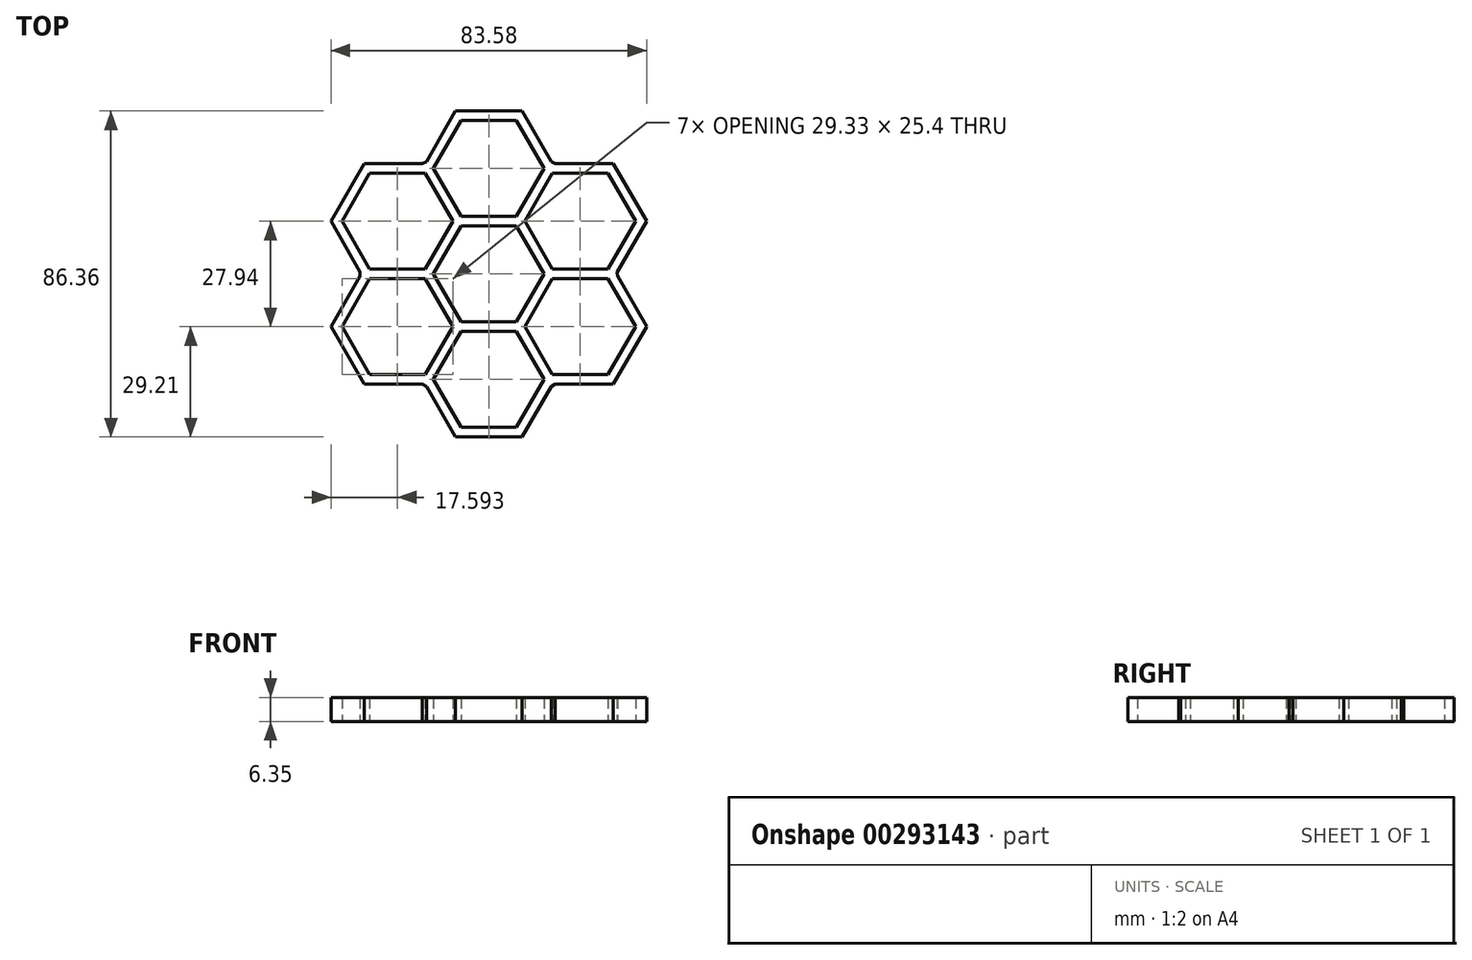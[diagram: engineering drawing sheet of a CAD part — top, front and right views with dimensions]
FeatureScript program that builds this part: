
annotation { "Feature Type Name" : "Feature", "Feature Type Description" : "" }
export const myFeature = defineFeature(function(context is Context, id is Id, definition is map)
    precondition{}
    {
        {
            var Q0;
            Q0=qCreatedBy(makeId("Top.planeOp"),FACE);
            var sketch = newSketch(context, id + "F0", { "sketchPlane" : qUnion([Q0])});
            skCircle(sketch, "E0.cCircle", {"center": v(0, 0) * mm, "radius": 12.7 * mm, "construction": true});
            skLineSegment(sketch, "E0.0", {"start": v(7.33, -12.7) * mm, "end": v(-7.33, -12.7) * mm});
            skLineSegment(sketch, "E0.1", {"start": v(-7.33, -12.7) * mm, "end": v(-14.66, 0) * mm});
            skLineSegment(sketch, "E0.2", {"start": v(-14.66, 0) * mm, "end": v(-7.33, 12.7) * mm});
            skLineSegment(sketch, "E0.3", {"start": v(-7.33, 12.7) * mm, "end": v(7.33, 12.7) * mm});
            skLineSegment(sketch, "E0.4", {"start": v(7.33, 12.7) * mm, "end": v(14.66, 0) * mm});
            skLineSegment(sketch, "E0.5", {"start": v(14.66, 0) * mm, "end": v(7.33, -12.7) * mm});
            skPoint(sketch, "E0.0.midPoint", {"position": v(0, -12.7) * mm});
            skCircle(sketch, "E1.cCircle", {"center": v(0, 27.94) * mm, "radius": 12.7 * mm, "construction": true});
            skLineSegment(sketch, "E1.0", {"start": v(7.33, 15.24) * mm, "end": v(-7.33, 15.24) * mm});
            skLineSegment(sketch, "E1.1", {"start": v(-7.33, 15.24) * mm, "end": v(-14.66, 27.94) * mm});
            skLineSegment(sketch, "E1.2", {"start": v(-14.66, 27.94) * mm, "end": v(-7.33, 40.64) * mm});
            skLineSegment(sketch, "E1.3", {"start": v(-7.33, 40.64) * mm, "end": v(7.33, 40.64) * mm});
            skLineSegment(sketch, "E1.4", {"start": v(7.33, 40.64) * mm, "end": v(14.66, 27.94) * mm});
            skLineSegment(sketch, "E1.5", {"start": v(14.66, 27.94) * mm, "end": v(7.33, 15.24) * mm});
            skPoint(sketch, "E1.0.midPoint", {"position": v(0, 15.24) * mm});
            skLineSegment(sketch, "E2.1.0", {"start": v(-31.53, 1.27) * mm, "end": v(-38.86, 13.97) * mm});
            skLineSegment(sketch, "E2.1.1", {"start": v(-38.86, 13.97) * mm, "end": v(-31.53, 26.67) * mm});
            skLineSegment(sketch, "E2.1.2", {"start": v(-31.53, 26.67) * mm, "end": v(-16.86, 26.67) * mm});
            skLineSegment(sketch, "E2.1.3", {"start": v(-16.86, 26.67) * mm, "end": v(-9.53, 13.97) * mm});
            skLineSegment(sketch, "E2.1.4", {"start": v(-9.53, 13.97) * mm, "end": v(-16.86, 1.27) * mm});
            skLineSegment(sketch, "E2.1.5", {"start": v(-16.86, 1.27) * mm, "end": v(-31.53, 1.27) * mm});
            skLineSegment(sketch, "E2.2.0", {"start": v(-16.86, -26.67) * mm, "end": v(-31.53, -26.67) * mm});
            skLineSegment(sketch, "E2.2.1", {"start": v(-31.53, -26.67) * mm, "end": v(-38.86, -13.97) * mm});
            skLineSegment(sketch, "E2.2.2", {"start": v(-38.86, -13.97) * mm, "end": v(-31.53, -1.27) * mm});
            skLineSegment(sketch, "E2.2.3", {"start": v(-31.53, -1.27) * mm, "end": v(-16.86, -1.27) * mm});
            skLineSegment(sketch, "E2.2.4", {"start": v(-16.86, -1.27) * mm, "end": v(-9.53, -13.97) * mm});
            skLineSegment(sketch, "E2.2.5", {"start": v(-9.53, -13.97) * mm, "end": v(-16.86, -26.67) * mm});
            skLineSegment(sketch, "E2.3.0", {"start": v(14.66, -27.94) * mm, "end": v(7.33, -40.64) * mm});
            skLineSegment(sketch, "E2.3.1", {"start": v(7.33, -40.64) * mm, "end": v(-7.33, -40.64) * mm});
            skLineSegment(sketch, "E2.3.2", {"start": v(-7.33, -40.64) * mm, "end": v(-14.66, -27.94) * mm});
            skLineSegment(sketch, "E2.3.3", {"start": v(-14.66, -27.94) * mm, "end": v(-7.33, -15.24) * mm});
            skLineSegment(sketch, "E2.3.4", {"start": v(-7.33, -15.24) * mm, "end": v(7.33, -15.24) * mm});
            skLineSegment(sketch, "E2.3.5", {"start": v(7.33, -15.24) * mm, "end": v(14.66, -27.94) * mm});
            skLineSegment(sketch, "E2.4.0", {"start": v(31.53, -1.27) * mm, "end": v(38.86, -13.97) * mm});
            skLineSegment(sketch, "E2.4.1", {"start": v(38.86, -13.97) * mm, "end": v(31.53, -26.67) * mm});
            skLineSegment(sketch, "E2.4.2", {"start": v(31.53, -26.67) * mm, "end": v(16.86, -26.67) * mm});
            skLineSegment(sketch, "E2.4.3", {"start": v(16.86, -26.67) * mm, "end": v(9.53, -13.97) * mm});
            skLineSegment(sketch, "E2.4.4", {"start": v(9.53, -13.97) * mm, "end": v(16.86, -1.27) * mm});
            skLineSegment(sketch, "E2.4.5", {"start": v(16.86, -1.27) * mm, "end": v(31.53, -1.27) * mm});
            skLineSegment(sketch, "E2.5.0", {"start": v(16.86, 26.67) * mm, "end": v(31.53, 26.67) * mm});
            skLineSegment(sketch, "E2.5.1", {"start": v(31.53, 26.67) * mm, "end": v(38.86, 13.97) * mm});
            skLineSegment(sketch, "E2.5.2", {"start": v(38.86, 13.97) * mm, "end": v(31.53, 1.27) * mm});
            skLineSegment(sketch, "E2.5.3", {"start": v(31.53, 1.27) * mm, "end": v(16.86, 1.27) * mm});
            skLineSegment(sketch, "E2.5.4", {"start": v(16.86, 1.27) * mm, "end": v(9.53, 13.97) * mm});
            skLineSegment(sketch, "E2.5.5", {"start": v(9.53, 13.97) * mm, "end": v(16.86, 26.67) * mm});
            skLineSegment(sketch, "E3", {"start": v(31.33, 1.4) * mm, "end": v(31.34, 1.27) * mm});
            skLineSegment(sketch, "E4.0", {"start": v(33, 29.21) * mm, "end": v(41.8, 13.97) * mm});
            skLineSegment(sketch, "E4.1", {"start": v(-17.54, -29.2) * mm, "end": v(-33, -29.2) * mm});
            skLineSegment(sketch, "E4.2", {"start": v(-17.54, -29.21) * mm, "end": v(-16.52, -29.8) * mm});
            skLineSegment(sketch, "E4.3", {"start": v(-8.8, -43.18) * mm, "end": v(-16.52, -29.8) * mm});
            skLineSegment(sketch, "E4.4", {"start": v(8.8, -43.18) * mm, "end": v(-8.8, -43.18) * mm});
            skLineSegment(sketch, "E4.5", {"start": v(16.52, -29.8) * mm, "end": v(8.8, -43.18) * mm});
            skLineSegment(sketch, "E4.6", {"start": v(17.54, -29.21) * mm, "end": v(16.52, -29.8) * mm});
            skLineSegment(sketch, "E4.7", {"start": v(33.95, 0.39) * mm, "end": v(34.02, -0.5) * mm});
            skLineSegment(sketch, "E4.8", {"start": v(34.02, -0.5) * mm, "end": v(41.8, -13.97) * mm});
            skLineSegment(sketch, "E4.9", {"start": v(41.8, -13.97) * mm, "end": v(33, -29.21) * mm});
            skLineSegment(sketch, "E4.10", {"start": v(33, -29.21) * mm, "end": v(17.54, -29.21) * mm});
            skLineSegment(sketch, "E4.11", {"start": v(-33, -29.2) * mm, "end": v(-41.8, -13.97) * mm});
            skLineSegment(sketch, "E4.12", {"start": v(41.8, 13.97) * mm, "end": v(33.95, 0.39) * mm});
            skLineSegment(sketch, "E4.13", {"start": v(-41.8, -13.97) * mm, "end": v(-34.07, -0.59) * mm});
            skLineSegment(sketch, "E4.14", {"start": v(-34.07, 0.59) * mm, "end": v(-34.07, -0.59) * mm});
            skLineSegment(sketch, "E4.15", {"start": v(-34.07, 0.59) * mm, "end": v(-41.8, 13.97) * mm});
            skLineSegment(sketch, "E4.16", {"start": v(-41.8, 13.97) * mm, "end": v(-33, 29.21) * mm});
            skLineSegment(sketch, "E4.17", {"start": v(-33, 29.21) * mm, "end": v(-17.54, 29.21) * mm});
            skLineSegment(sketch, "E4.18", {"start": v(-16.52, 29.8) * mm, "end": v(-17.54, 29.21) * mm});
            skLineSegment(sketch, "E4.19", {"start": v(-16.52, 29.8) * mm, "end": v(-8.8, 43.18) * mm});
            skLineSegment(sketch, "E4.20", {"start": v(-8.8, 43.18) * mm, "end": v(8.8, 43.18) * mm});
            skLineSegment(sketch, "E4.21", {"start": v(8.8, 43.18) * mm, "end": v(16.52, 29.8) * mm});
            skLineSegment(sketch, "E4.22", {"start": v(16.52, 29.8) * mm, "end": v(17.54, 29.21) * mm});
            skLineSegment(sketch, "E4.23", {"start": v(17.54, 29.21) * mm, "end": v(33, 29.21) * mm});
            skSolve(sketch);
        }
        {
            var Q0;
            Q0 = qSketchRegion(id + "F0", true);
            extrude(context, id + "F1", {"entities" : qUnion([Q0]), "depth" : 6.35 * mm});
        }
    });
